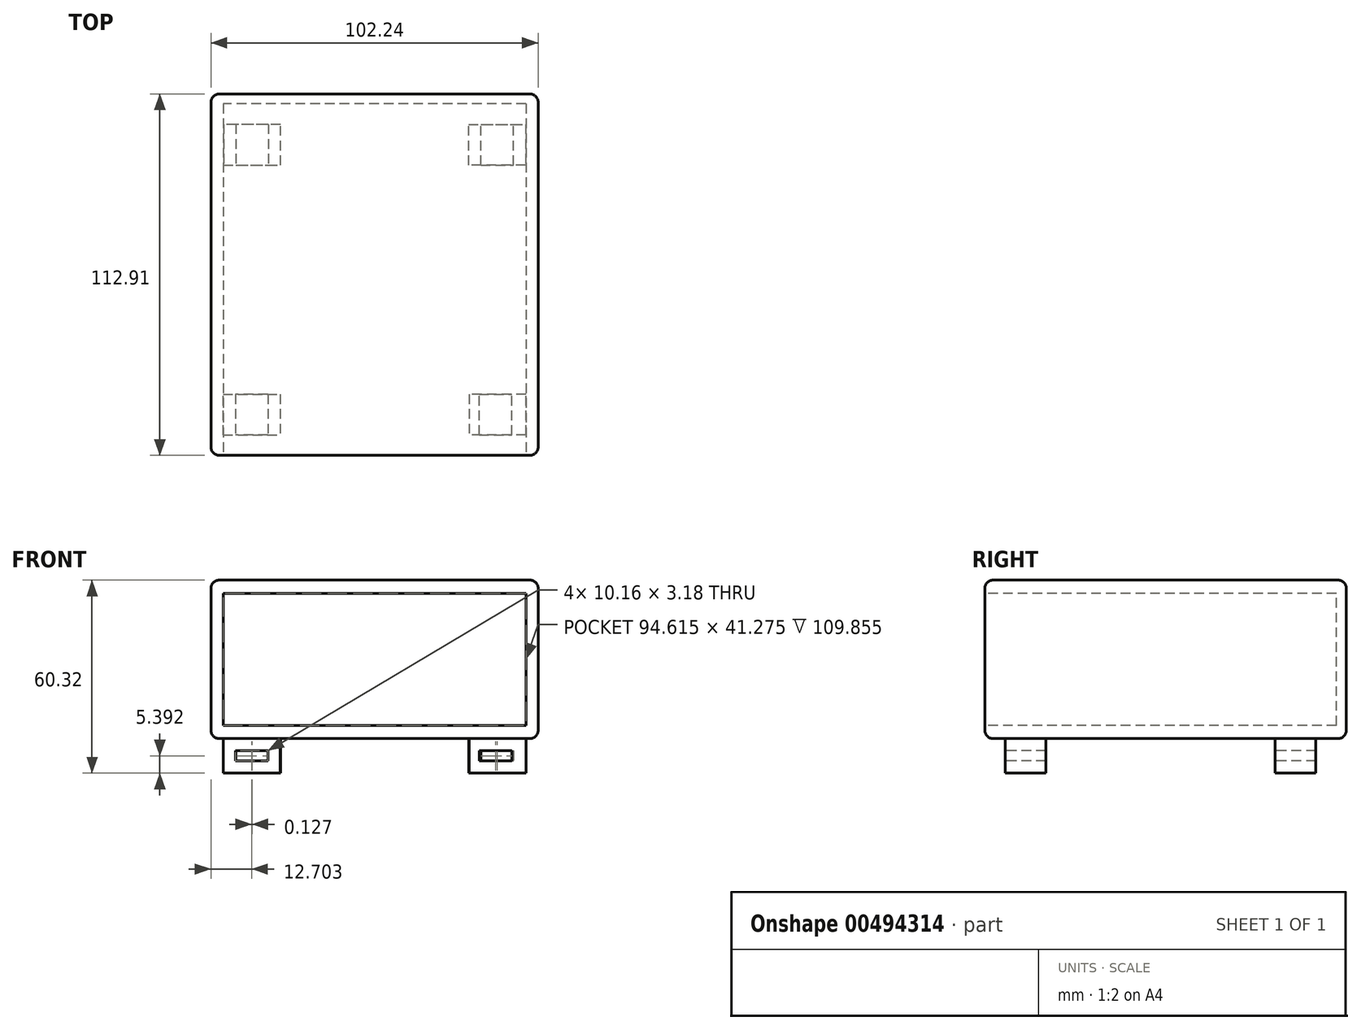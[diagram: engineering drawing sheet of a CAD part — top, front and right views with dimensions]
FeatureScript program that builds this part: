
annotation { "Feature Type Name" : "Feature", "Feature Type Description" : "" }
export const myFeature = defineFeature(function(context is Context, id is Id, definition is map)
    precondition{}
    {
        {
            var Q0;
            Q0=qCreatedBy(makeId("Top.planeOp"),FACE);
            var sketch = newSketch(context, id + "F0", { "sketchPlane" : qUnion([Q0])});
            skLineSegment(sketch, "E0.bottom", {"start": v(51.12, 54.93) * mm, "end": v(-51.12, 54.93) * mm});
            skLineSegment(sketch, "E0.top", {"start": v(51.12, -54.93) * mm, "end": v(-51.12, -54.93) * mm});
            skLineSegment(sketch, "E0.left", {"start": v(51.12, 54.93) * mm, "end": v(51.12, -54.93) * mm});
            skLineSegment(sketch, "E0.right", {"start": v(-51.12, 54.93) * mm, "end": v(-51.12, -54.93) * mm});
            skPoint(sketch, "E0.middle", {"position": v(0, 0) * mm});
            skSolve(sketch);
        }
        {
            var Q0;
            Q0=qSketchRegion(id+"F0",true);
            extrude(context, id + "F1", {"entities" : qUnion([Q0]), "depth" : 49.53 * mm, "offsetDistance" : 25.4 * mm});
        }
        {
            var Q0;
            Q0=makeQuery(id+"F1.opExtrude","SWEPT_FACE",FACE,{"disambiguationData":[OSD([sQuery(id+"F0.wireOp",EDGE,"E0.top")])]});
            var sketch = newSketch(context, id + "F2", { "sketchPlane" : qUnion([Q0])});
            skLineSegment(sketch, "E1.bottom", {"start": v(47.3, 4.13) * mm, "end": v(-47.3, 4.13) * mm});
            skLineSegment(sketch, "E1.top", {"start": v(47.3, 45.4) * mm, "end": v(-47.3, 45.4) * mm});
            skLineSegment(sketch, "E1.left", {"start": v(47.3, 4.13) * mm, "end": v(47.3, 45.4) * mm});
            skLineSegment(sketch, "E1.right", {"start": v(-47.3, 4.13) * mm, "end": v(-47.3, 45.4) * mm});
            skPoint(sketch, "E1.middle", {"position": v(0, 24.77) * mm});
            skPoint(sketch, "E1.middle.positionSnap0", {"position": v(51.12, 24.77) * mm});
            skPoint(sketch, "E1.centerSnap0", {"position": v(51.12, 24.77) * mm});
            skSolve(sketch);
        }
        {
            var Q0;
            Q0=qSketchRegion(id+"F2",true);
            extrude(context, id + "F3", {"entities" : qUnion([Q0]), "operationType" : NewBodyOperationType.REMOVE, "oppositeDirection" : true, "depth" : 111.25 * mm});
        }
        {
            var Q0;
            Q0=makeQuery(id+"Fa1ymK5Bm46zqyq_1.boolean.opBoolean","MERGE",FACE,{"derivedFrom":[makeQuery(id+"FQ6TK5hvAKRnzMb_1.boolean.opBoolean","MERGE",FACE,{"derivedFrom":[makeQuery(id+"F1.opExtrude","CAP_FACE",FACE,{"disambiguationData":[OSD([sQuery(id+"F0.wireOp",EDGE,"E0.bottom"),sQuery(id+"F0.wireOp",EDGE,"E0.top"),sQuery(id+"F0.wireOp",EDGE,"E0.left"),sQuery(id+"F0.wireOp",EDGE,"E0.right")])],"isStart":true}),makeQuery(id+"FQ6TK5hvAKRnzMb_1.opExtrude","SWEPT_FACE",FACE,{"disambiguationData":[OSD([sQuery(id+"FiJC8qJE0zteGb0_1.wireOp",EDGE,"P0wUqurH-Gj6t-9bPJ-ErCi-QS2WBkCEhN48")])]}),makeQuery(id+"FQ6TK5hvAKRnzMb_1.opExtrude","SWEPT_FACE",FACE,{"disambiguationData":[OSD([sQuery(id+"FiJC8qJE0zteGb0_1.wireOp",EDGE,"YM6bp2hf-gPkv-v1UY-YoXR-9SA9qtFhJgT4")])]})]}),makeQuery(id+"Fa1ymK5Bm46zqyq_1.opExtrude","SWEPT_FACE",FACE,{"disambiguationData":[OSD([sQuery(id+"FU2lz11TfoTLZVr_1.wireOp",EDGE,"Xva8lvJK-95PE-67xd-nmYC-munjzKADy0KN")])]}),makeQuery(id+"Fa1ymK5Bm46zqyq_1.opExtrude","SWEPT_FACE",FACE,{"disambiguationData":[OSD([sQuery(id+"FU2lz11TfoTLZVr_1.wireOp",EDGE,"3gXt7Lff-mfg9-Ye7T-QM5F-mXdbyLpD5R28")])]})]});
            var sketch = newSketch(context, id + "F4", { "sketchPlane" : qUnion([Q0])});
            skLineSegment(sketch, "E2.MirrorCS", {"start": v(-47.18, -35.78) * mm, "end": v(-29.4, -35.78) * mm});
            skLineSegment(sketch, "E3.MirrorCS", {"start": v(-29.4, -48.48) * mm, "end": v(-47.18, -48.48) * mm});
            skLineSegment(sketch, "E4.MirrorCS", {"start": v(-47.3, 48.58) * mm, "end": v(-47.3, 35.88) * mm});
            skLineSegment(sketch, "E5.MirrorCS", {"start": v(-29.53, 35.88) * mm, "end": v(-29.53, 48.58) * mm});
            skLineSegment(sketch, "E6.MirrorCS", {"start": v(-47.3, 35.88) * mm, "end": v(-29.53, 35.88) * mm});
            skLineSegment(sketch, "E7", {"start": v(-47.3, 48.58) * mm, "end": v(-29.53, 48.58) * mm});
            skLineSegment(sketch, "E8", {"start": v(-47.18, -48.48) * mm, "end": v(-47.18, -35.78) * mm});
            skLineSegment(sketch, "E9", {"start": v(-29.4, -35.78) * mm, "end": v(-29.4, -48.48) * mm});
            skLineSegment(sketch, "E10", {"start": v(-38.42, 54.93) * mm, "end": v(-38.42, 42.23) * mm});
            skLineSegment(sketch, "E11.0", {"start": v(51.12, 54.93) * mm, "end": v(-51.12, 54.93) * mm});
            skLineSegment(sketch, "E12.0", {"start": v(51.12, -54.93) * mm, "end": v(-51.12, -54.93) * mm});
            skLineSegment(sketch, "E13", {"start": v(51.12, 54.93) * mm, "end": v(38.42, 54.93) * mm});
            skLineSegment(sketch, "E14", {"start": v(38.42, 54.93) * mm, "end": v(38.42, 42.23) * mm});
            skLineSegment(sketch, "E15", {"start": v(51.12, -54.93) * mm, "end": v(38.42, -54.93) * mm});
            skLineSegment(sketch, "E16", {"start": v(38.42, -54.93) * mm, "end": v(38.42, -42.23) * mm});
            skLineSegment(sketch, "E17", {"start": v(0, 54.93) * mm, "end": v(0, -54.93) * mm});
            skLineSegment(sketch, "E18.MirrorCS", {"start": v(47.3, 48.58) * mm, "end": v(29.53, 48.58) * mm});
            skLineSegment(sketch, "E19.MirrorCS", {"start": v(47.3, 48.58) * mm, "end": v(47.3, 35.88) * mm});
            skLineSegment(sketch, "E20.MirrorCS", {"start": v(29.4, -48.48) * mm, "end": v(47.18, -48.48) * mm});
            skLineSegment(sketch, "E21.MirrorCS", {"start": v(47.18, -48.48) * mm, "end": v(47.18, -35.78) * mm});
            skLineSegment(sketch, "E22.MirrorCS", {"start": v(47.18, -35.78) * mm, "end": v(29.4, -35.78) * mm});
            skLineSegment(sketch, "E23.MirrorCS", {"start": v(29.4, -35.78) * mm, "end": v(29.4, -48.48) * mm});
            skLineSegment(sketch, "E24.MirrorCS", {"start": v(47.3, 35.88) * mm, "end": v(29.53, 35.88) * mm});
            skLineSegment(sketch, "E25.MirrorCS", {"start": v(29.53, 35.88) * mm, "end": v(29.53, 48.58) * mm});
            skSolve(sketch);
        }
        {
            var Q0;
            Q0=qSketchRegion(id+"F4",true);
            extrude(context, id + "F5", {"entities" : qUnion([Q0]), "operationType" : NewBodyOperationType.ADD, "depth" : 10.8 * mm, "offsetDistance" : 25.4 * mm});
        }
        {
            var Q0;
            Q0=makeQuery(id+"F5.boolean.opBoolean","MERGE",FACE,{"derivedFrom":[makeQuery(id+"F1.opExtrude","SWEPT_FACE",FACE,{"disambiguationData":[OSD([sQuery(id+"F0.wireOp",EDGE,"E0.right")])]}),makeQuery(id+"F5.opExtrude","SWEPT_FACE",FACE,{"disambiguationData":[OSD([sQuery(id+"F4.wireOp",EDGE,"E2.MirrorCS")])]}),makeQuery(id+"F5.opExtrude","SWEPT_FACE",FACE,{"disambiguationData":[OSD([sQuery(id+"F4.wireOp",EDGE,"074c0bec-36c9-46e3-96a0-11a15ca37a430.MirrorCS")])]})]});
            var sketch = newSketch(context, id + "F6", { "sketchPlane" : qUnion([Q0])});
            skLineSegment(sketch, "E26.bottom", {"start": v(-21.9, -1.59) * mm, "end": v(-32.07, -1.59) * mm});
            skLineSegment(sketch, "E26.top", {"start": v(-21.9, -4.76) * mm, "end": v(-32.07, -4.76) * mm});
            skLineSegment(sketch, "E26.left", {"start": v(-21.9, -1.59) * mm, "end": v(-21.9, -4.76) * mm});
            skLineSegment(sketch, "E26.right", {"start": v(-32.07, -1.59) * mm, "end": v(-32.07, -4.76) * mm});
            skPoint(sketch, "E26.middle", {"position": v(-26.99, -3.18) * mm});
            skLineSegment(sketch, "E27", {"start": v(0, 0) * mm, "end": v(0, -11.74) * mm});
            skLineSegment(sketch, "E28.MirrorCS", {"start": v(21.9, -1.59) * mm, "end": v(32.07, -1.59) * mm});
            skLineSegment(sketch, "E29.MirrorCS", {"start": v(32.07, -1.59) * mm, "end": v(32.07, -4.76) * mm});
            skLineSegment(sketch, "E30.MirrorCS", {"start": v(21.9, -1.59) * mm, "end": v(21.9, -4.76) * mm});
            skLineSegment(sketch, "E31.MirrorCS", {"start": v(21.9, -4.76) * mm, "end": v(32.07, -4.76) * mm});
            skSolve(sketch);
        }
        {
            var Q0;
            Q0=qSketchRegion(id+"F6",true);
            extrude(context, id + "F7", {"entities" : qUnion([Q0]), "operationType" : NewBodyOperationType.REMOVE, "oppositeDirection" : true, "depth" : 12.7 * mm});
        }
        {
            var Q0;
            Q0=makeQuery(id+"F1.opExtrude","SWEPT_FACE",FACE,{"disambiguationData":[OSD([sQuery(id+"F0.wireOp",EDGE,"E0.bottom")])]});
            var sketch = newSketch(context, id + "F8", { "sketchPlane" : qUnion([Q0])});
            skLineSegment(sketch, "E32", {"start": v(-51.12, 49.53) * mm, "end": v(51.12, 49.53) * mm});
            skLineSegment(sketch, "E33", {"start": v(51.12, 49.53) * mm, "end": v(51.12, 0) * mm});
            skLineSegment(sketch, "E34", {"start": v(51.12, 0) * mm, "end": v(-51.12, 0) * mm});
            skLineSegment(sketch, "E35", {"start": v(-51.12, 0) * mm, "end": v(-51.12, 49.53) * mm});
            skSolve(sketch);
        }
        {
            var Q0;
            Q0=qSketchRegion(id+"F8",true);
            extrude(context, id + "F9", {"entities" : qUnion([Q0]), "operationType" : NewBodyOperationType.ADD, "depth" : 3.05 * mm, "offsetDistance" : 25.4 * mm});
        }
        {
            var Q0;
            Q0=makeQuery(id+"F5.opExtrude","SWEPT_FACE",FACE,{"disambiguationData":[OSD([sQuery(id+"F4.wireOp",EDGE,"E7")])]});
            var sketch = newSketch(context, id + "F10", { "sketchPlane" : qUnion([Q0])});
            skLineSegment(sketch, "E36.0", {"start": v(-43.5, -6.99) * mm, "end": v(-43.5, -3.8) * mm});
            skLineSegment(sketch, "E37.0", {"start": v(-43.5, -3.81) * mm, "end": v(-33.34, -3.81) * mm});
            skLineSegment(sketch, "E38.0", {"start": v(-33.34, -3.8) * mm, "end": v(-33.34, -6.99) * mm});
            skLineSegment(sketch, "E39.0", {"start": v(-33.34, -6.99) * mm, "end": v(-43.5, -6.99) * mm});
            skLineSegment(sketch, "E40.0", {"start": v(-47.3, -10.8) * mm, "end": v(-29.53, -10.8) * mm});
            skLineSegment(sketch, "E40.1", {"start": v(-47.3, -10.8) * mm, "end": v(-47.3, 0) * mm});
            skLineSegment(sketch, "E40.2", {"start": v(-47.3, 0) * mm, "end": v(-29.53, 0) * mm});
            skLineSegment(sketch, "E40.3", {"start": v(-29.53, -10.8) * mm, "end": v(-29.53, 0) * mm});
            skSolve(sketch);
        }
        {
            var Q0;
            Q0=makeQuery(id+"F10.imprint","IMPRINT",FACE,{"disambiguationData":[TD([[makeQuery(id+"F10.imprint","IMPRINT",EDGE,{"derivedFrom":sQuery(id+"F10.wireOp",EDGE,"E36.0")}),-1.0]])]});
            extrude(context, id + "F11", {"entities" : qUnion([Q0]), "operationType" : NewBodyOperationType.REMOVE, "oppositeDirection" : true, "depth" : 25.4 * mm, "offsetDistance" : 25.4 * mm});
        }
        {
            var Q0;
            Q0=makeQuery(id+"F5.opExtrude","SWEPT_FACE",FACE,{"disambiguationData":[OSD([sQuery(id+"F4.wireOp",EDGE,"E2.MirrorCS")])]});
            var sketch = newSketch(context, id + "F12", { "sketchPlane" : qUnion([Q0])});
            skLineSegment(sketch, "E41.0.0", {"start": v(-47.18, 0) * mm, "end": v(-47.18, 0) * mm});
            skLineSegment(sketch, "E41.0.1", {"start": v(-47.18, 0) * mm, "end": v(-47.18, -10.8) * mm});
            skLineSegment(sketch, "E41.0.2", {"start": v(-47.18, -10.8) * mm, "end": v(-47.18, -10.8) * mm});
            skLineSegment(sketch, "E41.0.3", {"start": v(-47.18, 0) * mm, "end": v(-47.18, -10.8) * mm});
            skLineSegment(sketch, "E42.0", {"start": v(-33.21, -3.81) * mm, "end": v(-43.37, -3.81) * mm});
            skLineSegment(sketch, "E43.0", {"start": v(-43.37, -6.99) * mm, "end": v(-33.21, -6.99) * mm});
            skLineSegment(sketch, "E44.0", {"start": v(-33.21, -6.99) * mm, "end": v(-33.21, -3.8) * mm});
            skLineSegment(sketch, "E45.0", {"start": v(-43.37, -3.8) * mm, "end": v(-43.37, -6.99) * mm});
            skLineSegment(sketch, "E46.0.0", {"start": v(-47.3, 0) * mm, "end": v(-29.53, 0) * mm});
            skLineSegment(sketch, "E46.0.1", {"start": v(-29.53, 0) * mm, "end": v(-29.53, -10.8) * mm});
            skLineSegment(sketch, "E46.0.2", {"start": v(-29.53, -10.8) * mm, "end": v(-47.3, -10.8) * mm});
            skLineSegment(sketch, "E46.0.3", {"start": v(-47.3, -10.8) * mm, "end": v(-47.3, 0) * mm});
            skSolve(sketch);
        }
        {
            var Q0;
            Q0=makeQuery(id+"F12.imprint","IMPRINT",FACE,{"disambiguationData":[TD([[makeQuery(id+"F12.imprint","IMPRINT",EDGE,{"derivedFrom":sQuery(id+"F12.wireOp",EDGE,"E42.0")}),1.0]])]});
            extrude(context, id + "F13", {"entities" : qUnion([Q0]), "operationType" : NewBodyOperationType.REMOVE, "oppositeDirection" : true, "depth" : 25.4 * mm, "offsetDistance" : 25.4 * mm});
        }
        {
            var Q0;
            Q0=makeQuery(id+"F1.opExtrude","SWEPT_EDGE",EDGE,{"disambiguationData":[OSD([sQuery(id+"F0.wireOp",EDGE,"E0.top"),sQuery(id+"F0.wireOp",EDGE,"E0.right")])]});
            var Q1;
            Q1=makeQuery(id+"F1.opExtrude","SWEPT_EDGE",EDGE,{"disambiguationData":[OSD([sQuery(id+"F0.wireOp",EDGE,"E0.top"),sQuery(id+"F0.wireOp",EDGE,"E0.left")])]});
            var Q2;
            Q2=makeQuery(id+"F9.opExtrude","CAP_EDGE",EDGE,{"disambiguationData":[OSD([sQuery(id+"F8.wireOp",EDGE,"E35")])],"isStart":false});
            var Q3;
            Q3=makeQuery(id+"F9.opExtrude","CAP_EDGE",EDGE,{"disambiguationData":[OSD([sQuery(id+"F8.wireOp",EDGE,"E33")])],"isStart":false});
            var Q4;
            Q4=makeQuery(id+"F9.opExtrude","CAP_EDGE",EDGE,{"disambiguationData":[OSD([sQuery(id+"F8.wireOp",EDGE,"E34")])],"isStart":false});
            var Q5;
            Q5=makeQuery(id+"F9.boolean.opBoolean","MERGE",EDGE,{"derivedFrom":[makeQuery(id+"F1.opExtrude","CAP_EDGE",EDGE,{"disambiguationData":[OSD([sQuery(id+"F0.wireOp",EDGE,"E0.left")])],"isStart":true}),makeQuery(id+"F9.opExtrude","SWEPT_EDGE",EDGE,{"disambiguationData":[OSD([sQuery(id+"F8.wireOp",EDGE,"E34"),sQuery(id+"F8.wireOp",EDGE,"E35")])]})]});
            var Q6;
            Q6=makeQuery(id+"F9.boolean.opBoolean","MERGE",EDGE,{"derivedFrom":[makeQuery(id+"F1.opExtrude","CAP_EDGE",EDGE,{"disambiguationData":[OSD([sQuery(id+"F0.wireOp",EDGE,"E0.left")])],"isStart":false}),makeQuery(id+"F9.opExtrude","SWEPT_EDGE",EDGE,{"disambiguationData":[OSD([sQuery(id+"F8.wireOp",EDGE,"E32"),sQuery(id+"F8.wireOp",EDGE,"E35")])]})]});
            var Q7;
            Q7=makeQuery(id+"F9.boolean.opBoolean","MERGE",EDGE,{"derivedFrom":[makeQuery(id+"F1.opExtrude","CAP_EDGE",EDGE,{"disambiguationData":[OSD([sQuery(id+"F0.wireOp",EDGE,"E0.right")])],"isStart":true}),makeQuery(id+"F9.opExtrude","SWEPT_EDGE",EDGE,{"disambiguationData":[OSD([sQuery(id+"F8.wireOp",EDGE,"E33"),sQuery(id+"F8.wireOp",EDGE,"E34")])]})]});
            var Q8;
            Q8=makeQuery(id+"F9.boolean.opBoolean","MERGE",EDGE,{"derivedFrom":[makeQuery(id+"F1.opExtrude","CAP_EDGE",EDGE,{"disambiguationData":[OSD([sQuery(id+"F0.wireOp",EDGE,"E0.right")])],"isStart":false}),makeQuery(id+"F9.opExtrude","SWEPT_EDGE",EDGE,{"disambiguationData":[OSD([sQuery(id+"F8.wireOp",EDGE,"E32"),sQuery(id+"F8.wireOp",EDGE,"E33")])]})]});
            var Q9;
            Q9=makeQuery(id+"F9.opExtrude","CAP_EDGE",EDGE,{"disambiguationData":[OSD([sQuery(id+"F8.wireOp",EDGE,"E32")])],"isStart":false});
            var Q10;
            Q10=makeQuery(id+"F1.opExtrude","CAP_EDGE",EDGE,{"disambiguationData":[OSD([sQuery(id+"F0.wireOp",EDGE,"E0.top")])],"isStart":false});
            var Q11;
            Q11=makeQuery(id+"F1.opExtrude","CAP_EDGE",EDGE,{"disambiguationData":[OSD([sQuery(id+"F0.wireOp",EDGE,"E0.top")])],"isStart":true});
            fillet(context, id + "F14", {"entities" : qUnion([Q0, Q1, Q2, Q3, Q4, Q5, Q6, Q7, Q8, Q9, Q10, Q11]), "radius" : 2.54 * mm, "tangentPropagation" : true, "allowEdgeOverflow" : false});
        }
        {
            var Q0;
            Q0=makeQuery(id+"F5.opExtrude","SWEPT_FACE",FACE,{"disambiguationData":[OSD([sQuery(id+"F4.wireOp",EDGE,"E20.MirrorCS")])]});
            var sketch = newSketch(context, id + "F15", { "sketchPlane" : qUnion([Q0])});
            skLineSegment(sketch, "E47.0.0", {"start": v(-29.4, 0) * mm, "end": v(-47.18, 0) * mm});
            skLineSegment(sketch, "E47.0.1", {"start": v(-47.18, 0) * mm, "end": v(-47.18, -10.8) * mm});
            skLineSegment(sketch, "E47.0.2", {"start": v(-47.18, -10.8) * mm, "end": v(-29.4, -10.8) * mm});
            skLineSegment(sketch, "E47.0.3", {"start": v(-29.4, -10.8) * mm, "end": v(-29.4, 0) * mm});
            skPoint(sketch, "E48.firstSnap0", {"position": v(-29.4, -5.4) * mm});
            skPoint(sketch, "E48.firstSnap1", {"position": v(-38.3, -10.8) * mm});
            skLineSegment(sketch, "E48.bottom", {"start": v(-33.21, -3.8) * mm, "end": v(-43.37, -3.8) * mm});
            skLineSegment(sketch, "E48.top", {"start": v(-33.21, -6.98) * mm, "end": v(-43.37, -6.99) * mm});
            skLineSegment(sketch, "E48.left", {"start": v(-33.21, -3.8) * mm, "end": v(-33.21, -6.98) * mm});
            skLineSegment(sketch, "E48.right", {"start": v(-43.37, -3.81) * mm, "end": v(-43.37, -6.99) * mm});
            skSolve(sketch);
        }
        {
            var Q0;
            Q0=makeQuery(id+"F15.imprint","IMPRINT",FACE,{"disambiguationData":[TD([[makeQuery(id+"F15.imprint","IMPRINT",EDGE,{"derivedFrom":sQuery(id+"F15.wireOp",EDGE,"E48.bottom")}),1.0]])]});
            extrude(context, id + "F16", {"entities" : qUnion([Q0]), "operationType" : NewBodyOperationType.REMOVE, "oppositeDirection" : true, "depth" : 25.4 * mm, "offsetDistance" : 25.4 * mm});
        }
        {
            var Q0;
            Q0=makeQuery(id+"F5.opExtrude","SWEPT_FACE",FACE,{"disambiguationData":[OSD([sQuery(id+"F4.wireOp",EDGE,"E24.MirrorCS")])]});
            var sketch = newSketch(context, id + "F17", { "sketchPlane" : qUnion([Q0])});
            skLineSegment(sketch, "E49.0", {"start": v(-47.3, -10.8) * mm, "end": v(-29.53, -10.8) * mm});
            skPoint(sketch, "E50.endSnap0", {"position": v(-29.53, -5.4) * mm});
            skLineSegment(sketch, "E51.bottom", {"start": v(-32.7, -3.81) * mm, "end": v(-42.86, -3.81) * mm});
            skLineSegment(sketch, "E51.top", {"start": v(-32.7, -6.99) * mm, "end": v(-42.86, -6.99) * mm});
            skLineSegment(sketch, "E51.left", {"start": v(-32.7, -3.8) * mm, "end": v(-32.7, -6.98) * mm});
            skLineSegment(sketch, "E51.right", {"start": v(-42.86, -3.81) * mm, "end": v(-42.86, -6.99) * mm});
            skSolve(sketch);
        }
        {
            var Q0;
            Q0=makeQuery(id+"F17.imprint","IMPRINT",FACE,{"disambiguationData":[TD([[makeQuery(id+"F17.imprint","IMPRINT",EDGE,{"derivedFrom":sQuery(id+"F17.wireOp",EDGE,"E51.bottom")}),1.0]])]});
            extrude(context, id + "F18", {"entities" : qUnion([Q0]), "operationType" : NewBodyOperationType.REMOVE, "oppositeDirection" : true, "depth" : 25.4 * mm, "offsetDistance" : 25.4 * mm});
        }
    });
